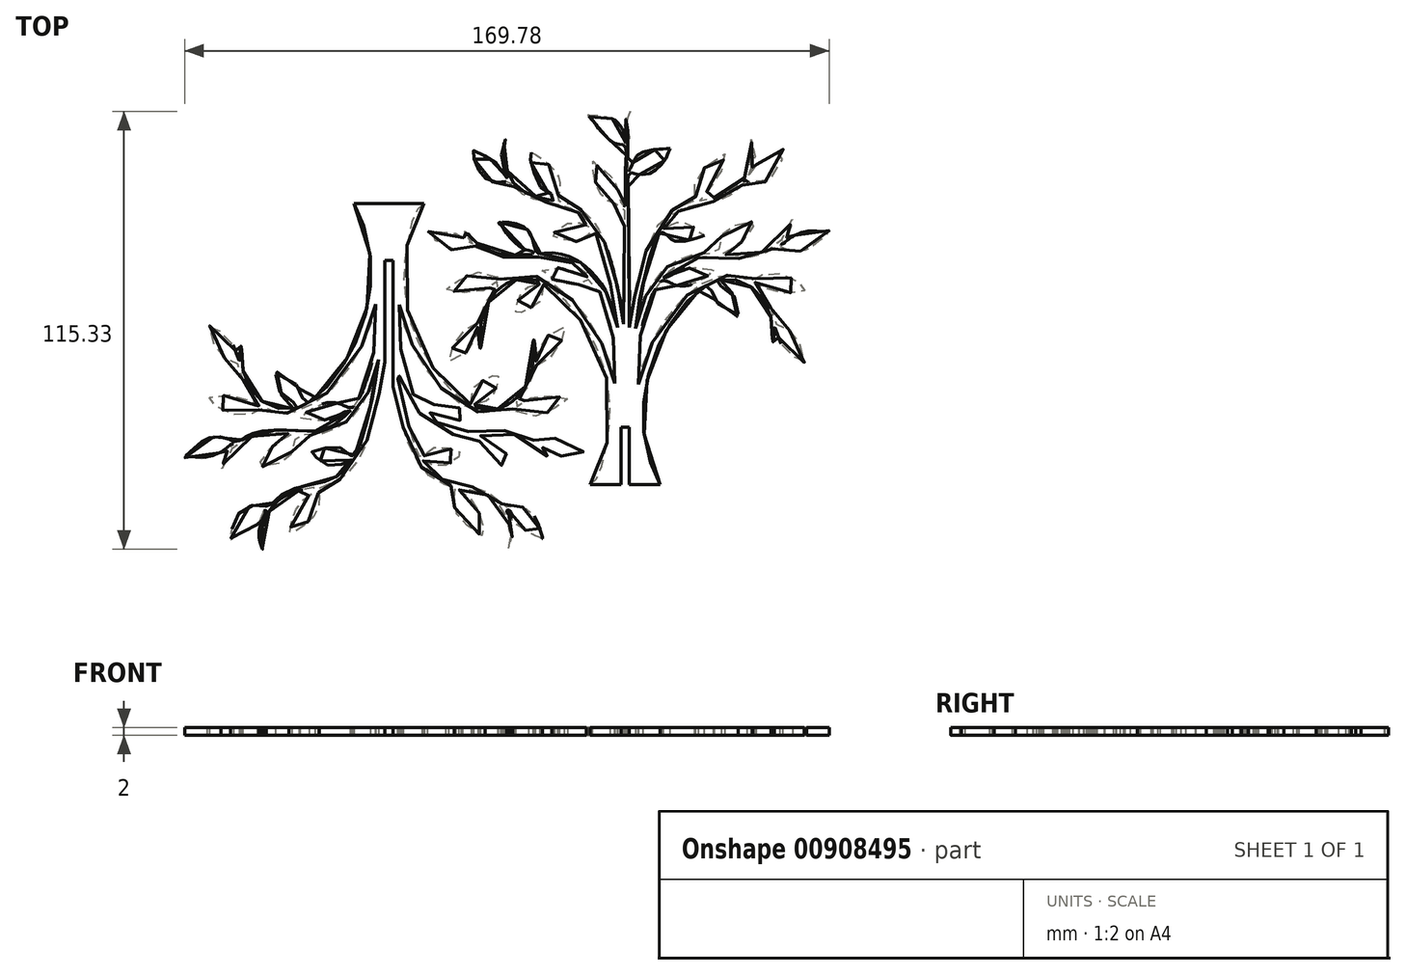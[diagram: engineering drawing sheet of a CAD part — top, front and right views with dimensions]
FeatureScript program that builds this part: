
annotation { "Feature Type Name" : "Feature", "Feature Type Description" : "" }
export const myFeature = defineFeature(function(context is Context, id is Id, definition is map)
    precondition{}
    {
        {
            var Q0;
            Q0=qCreatedBy(makeId("Top.planeOp"),FACE);
            var sketch = newSketch(context, id + "F0", { "sketchPlane" : qUnion([Q0])});
            skLineSegment(sketch, "E0", {"start": v(29.95, -44.14) * mm, "end": v(21.84, -44.14) * mm});
            skLineSegment(sketch, "E1.left", {"start": v(19.69, -28.94) * mm, "end": v(19.69, -44.14) * mm});
            skLineSegment(sketch, "E1.right", {"start": v(21.84, -28.94) * mm, "end": v(21.84, -44.14) * mm});
            skLineSegment(sketch, "E2", {"start": v(20.76, -44.14) * mm, "end": v(20.76, -22.34) * mm, "construction": true});
            skLineSegment(sketch, "E3.trimOffspring", {"start": v(19.69, -44.14) * mm, "end": v(11.58, -44.14) * mm});
            skLineSegment(sketch, "E4", {"start": v(19.69, -28.94) * mm, "end": v(21.84, -28.94) * mm});
            skFitSpline(sketch, "E5", {"points": [v(20.33, -1.79) * mm, v(20.33, 0) * mm, v(20.33, 5.52) * mm, v(20.5, 10.68) * mm, v(20.54, 16.14) * mm, v(20.63, 24.42) * mm, v(20.68, 28.14) * mm, v(20.56, 28.4) * mm, v(19.58, 29.1) * mm, v(18.8, 29.58) * mm, v(17.17, 30.16) * mm, v(15.4, 31.25) * mm, v(14.15, 32.69) * mm, v(13.3, 34.38) * mm, v(12.64, 36.54) * mm, v(12.27, 38.87) * mm, v(12.25, 41.19) * mm, v(12.34, 40.84) * mm, v(13.34, 39.96) * mm, v(15.38, 38.54) * mm, v(17.08, 37.03) * mm, v(18.33, 34.76) * mm, v(19.08, 32.67) * mm, v(19.54, 30.72) * mm, v(19.68, 30.05) * mm, v(19.94, 29.68) * mm, v(20.34, 29.42) * mm, v(20.66, 29.27) * mm, v(20.8, 29.32) * mm, v(20.82, 34.1) * mm, v(20.84, 38.03) * mm, v(20.98, 44.37) * mm, v(20.84, 44.72) * mm, v(20.33, 45.32) * mm, v(18.54, 45.7) * mm, v(16.85, 46.5) * mm, v(14.64, 48.66) * mm, v(13.71, 49.78) * mm, v(12.53, 51.47) * mm, v(11.78, 52.38) * mm, v(10.93, 53.24) * mm, v(11.32, 53.24) * mm, v(12.6, 53.24) * mm, v(14.97, 52.91) * mm, v(17.45, 52.24) * mm, v(18.96, 51.1) * mm, v(20.33, 48.85) * mm, v(20.77, 47.18) * mm, v(20.89, 46.37) * mm, v(20.89, 45.72) * mm, v(21.1, 45.58) * mm, v(21.3, 46.46) * mm, v(20.96, 49.08) * mm, v(20.77, 51.54) * mm, v(22.1, 54.21) * mm, v(21.9, 53.63) * mm, v(21.23, 51.98) * mm, v(21.26, 49.9) * mm, v(21.72, 47.8) * mm, v(21.8, 46.09) * mm, v(21.42, 44.58) * mm, v(21.51, 43.2) * mm, v(21.47, 40.89) * mm, v(21.5, 39.14) * mm, v(21.51, 38.22) * mm, v(21.82, 38.61) * mm, v(22.44, 40) * mm, v(23.44, 41.95) * mm, v(24.5, 43) * mm, v(25.83, 43.63) * mm, v(27.5, 44.02) * mm, v(29.7, 44.28) * mm, v(32.68, 44.37) * mm, v(32.54, 44.28) * mm, v(32.17, 43.49) * mm, v(31.5, 41.84) * mm, v(30.03, 39.86) * mm, v(28.57, 38.56) * mm, v(26.57, 37.66) * mm, v(24.62, 37.61) * mm, v(23.56, 37.73) * mm, v(22.37, 38.05) * mm, v(22.14, 37.82) * mm, v(21.51, 37.22) * mm, v(21.44, 35.85) * mm, v(21.56, 32.92) * mm, v(21.58, 30.11) * mm, v(21.65, 24.28) * mm, v(21.7, 18.8) * mm, v(21.77, 11.03) * mm, v(21.9, 6.5) * mm, v(21.84, 1.53) * mm, v(21.82, -2.7) * mm], "startDerivative": vector(0.58, 144) * mm, "endDerivative": vector(0.16, -253) * mm});
            skFitSpline(sketch, "E6", {"points": [v(21.82, -2.7) * mm, v(22.07, -2.06) * mm, v(22.19, -1.2) * mm, v(22.25, 0.23) * mm, v(22.62, 2.54) * mm, v(23.19, 5.31) * mm, v(24.24, 10.2) * mm, v(25.16, 13.53) * mm, v(26.2, 17.34) * mm, v(28.25, 22.4) * mm, v(30.9, 26.17) * mm, v(33.24, 28.2) * mm, v(35.34, 29.42) * mm, v(37.8, 30.2) * mm, v(39.05, 30.44) * mm, v(39.21, 30.93) * mm, v(39.4, 31.69) * mm, v(39.25, 32.25) * mm, v(39.08, 34.12) * mm, v(39.34, 36.05) * mm, v(40.13, 37.73) * mm, v(41.68, 39.4) * mm, v(43.71, 41.14) * mm, v(45.25, 42.16) * mm, v(47.1, 43.05) * mm, v(46.96, 42.79) * mm, v(46.63, 41.37) * mm, v(46.27, 39.34) * mm, v(45.35, 36.8) * mm, v(44.33, 35.1) * mm, v(42.04, 32.93) * mm, v(40.66, 31.98) * mm, v(40.27, 31.45) * mm, v(40.17, 30.74) * mm, v(40.5, 30.67) * mm, v(42.46, 31.1) * mm, v(45.1, 31.62) * mm, v(47.45, 32.57) * mm, v(49.75, 33.99) * mm, v(51.46, 35.66) * mm, v(52.68, 37.6) * mm, v(53.56, 39.53) * mm, v(54.15, 41.3) * mm, v(54.38, 43.5) * mm, v(54.02, 46.92) * mm, v(54.32, 46.36) * mm, v(54.78, 44.85) * mm, v(54.97, 42.65) * mm, v(54.38, 39.8) * mm, v(53.17, 37.3) * mm, v(53.02, 36.83) * mm, v(53.39, 36.67) * mm, v(53.82, 36.97) * mm, v(54.48, 38.65) * mm, v(55.53, 40.39) * mm, v(58.16, 42.1) * mm, v(60.33, 43.08) * mm, v(62.03, 44) * mm, v(62.3, 44.5) * mm, v(62.4, 43.54) * mm, v(61.77, 40.62) * mm, v(60.65, 37.93) * mm, v(58.52, 36.02) * mm, v(56.09, 35.27) * mm, v(53.8, 35.3) * mm, v(53, 35.73) * mm, v(52.64, 35.99) * mm, v(52.38, 36.02) * mm, v(52.12, 35.63) * mm, v(50.93, 34.22) * mm, v(49.33, 32.87) * mm, v(47.65, 31.69) * mm, v(45.62, 30.93) * mm, v(43.48, 30.37) * mm, v(39.84, 29.68) * mm, v(38.65, 29.39) * mm, v(36.62, 28.76) * mm, v(34.81, 27.98) * mm, v(33.3, 26.9) * mm, v(32.38, 26.04) * mm, v(31, 24.66) * mm, v(30.31, 23.64) * mm, v(30.58, 23.38) * mm, v(30.97, 23.38) * mm, v(31.99, 24.04) * mm, v(33.8, 24.76) * mm, v(35.3, 25.12) * mm, v(37.93, 24.23) * mm, v(39.34, 23.22) * mm, v(40.62, 22.13) * mm, v(41.6, 21.57) * mm, v(40.89, 21.25) * mm, v(39.11, 20.69) * mm, v(36.72, 20.1) * mm, v(34.52, 20.03) * mm, v(32.97, 20.5) * mm, v(31.04, 22.16) * mm, v(29.64, 22.16) * mm, v(28.74, 20.46) * mm, v(27.36, 16.22) * mm, v(25.5, 8.8) * mm, v(24.67, 5.06) * mm, v(24, 0.79) * mm, v(23.48, -2.99) * mm], "startDerivative": vector(50.29, 106) * mm, "endDerivative": vector(-37.17, -267.82) * mm});
            skFitSpline(sketch, "E7", {"points": [v(23.48, -2.99) * mm, v(23.78, -2.7) * mm, v(24.1, -1.08) * mm, v(24.67, 1.95) * mm, v(26.08, 5.29) * mm, v(27.59, 8.18) * mm, v(28.48, 9.59) * mm, v(30.7, 12.25) * mm, v(33.33, 14.35) * mm, v(36.55, 16.06) * mm, v(39.77, 16.85) * mm, v(42.73, 16.91) * mm, v(45.06, 16.75) * mm, v(45.52, 17.53) * mm, v(45.65, 19.28) * mm, v(46.63, 22.03) * mm, v(47.78, 23.35) * mm, v(49.56, 24.27) * mm, v(52.18, 24.99) * mm, v(55.33, 25.15) * mm, v(55.04, 24.92) * mm, v(54.48, 23.84) * mm, v(52.6, 21.25) * mm, v(51.2, 19.57) * mm, v(49.13, 18.06) * mm, v(46.38, 17.29) * mm, v(46.21, 16.81) * mm, v(46.34, 16.52) * mm, v(47.75, 16.45) * mm, v(50.5, 16.32) * mm, v(53.7, 16.48) * mm, v(56.16, 16.98) * mm, v(59.08, 18.22) * mm, v(61.4, 20.03) * mm, v(63.41, 22.2) * mm, v(65.02, 26.66) * mm, v(64.99, 26.14) * mm, v(64.73, 24.33) * mm, v(63.87, 21.93) * mm, v(62.76, 20.42) * mm, v(61.61, 19.48) * mm, v(61.62, 19.3) * mm, v(61.74, 19.2) * mm, v(62.3, 19.3) * mm, v(63.97, 20.65) * mm, v(67.71, 22.43) * mm, v(70.9, 22.7) * mm, v(73.4, 22.6) * mm, v(74.51, 22.82) * mm, v(73.36, 21.4) * mm, v(70.5, 18.98) * mm, v(68.6, 17.76) * mm, v(65.32, 17.3) * mm, v(62.76, 18.03) * mm, v(61.97, 18.49) * mm, v(60.65, 18.65) * mm, v(59.9, 18.2) * mm, v(58.59, 17.37) * mm, v(56.85, 16.58) * mm, v(53.89, 15.8) * mm, v(49.5, 15.5) * mm, v(45.06, 15.66) * mm, v(42.17, 15.86) * mm, v(39.84, 15.73) * mm, v(36.75, 14.9) * mm, v(34.02, 13.36) * mm, v(30.87, 10.48) * mm, v(31, 10.48) * mm, v(31.71, 10.5) * mm, v(33.3, 11.33) * mm, v(35.8, 12.54) * mm, v(37.7, 12.94) * mm, v(40.72, 12.9) * mm, v(44.3, 12.28) * mm, v(43.8, 12.18) * mm, v(42.6, 10.93) * mm, v(40.4, 9.65) * mm, v(37.93, 8.54) * mm, v(35.93, 8.24) * mm, v(33.93, 8.54) * mm, v(32.07, 9.3) * mm, v(31.3, 9.56) * mm, v(30.4, 9.58) * mm, v(29.82, 9.06) * mm, v(28.15, 6.37) * mm, v(27.2, 4) * mm, v(25.13, -2.7) * mm, v(24.44, -7.85) * mm, v(24.24, -14.25) * mm, v(24.27, -17.63) * mm], "startDerivative": vector(65.15, 43.2) * mm, "endDerivative": vector(4.6, -218.26) * mm});
            skFitSpline(sketch, "E8", {"points": [v(24.27, -17.63) * mm, v(24.67, -15.33) * mm, v(26.47, -9.72) * mm, v(28.21, -5.98) * mm, v(32.42, 0.66) * mm, v(37.24, 6.04) * mm, v(41.12, 9) * mm, v(45.12, 10.67) * mm, v(49.06, 11.03) * mm, v(51.79, 10.38) * mm, v(53, 9.65) * mm, v(53.66, 9.65) * mm, v(54.97, 10.11) * mm, v(56.88, 11.2) * mm, v(60.16, 11.76) * mm, v(63.35, 10.87) * mm, v(66.8, 9) * mm, v(68.6, 7.39) * mm, v(68.24, 6.96) * mm, v(64.53, 6.47) * mm, v(60.65, 6.4) * mm, v(56.78, 8.18) * mm, v(55.56, 9.09) * mm, v(54.72, 9.07) * mm, v(54.37, 8.75) * mm, v(55.2, 8) * mm, v(57.63, 5.32) * mm, v(59.2, 1.95) * mm, v(60.03, -1.15) * mm, v(60.95, -2.13) * mm, v(62.3, -2.7) * mm, v(64.89, -4.07) * mm, v(66.5, -6.44) * mm, v(67.29, -9) * mm, v(67.98, -11.92) * mm, v(67.75, -11.69) * mm, v(65.8, -10.74) * mm, v(63.12, -9.06) * mm, v(61.11, -5.06) * mm, v(60.4, -2.99) * mm, v(60.15, -2.76) * mm, v(60.1, -3.6) * mm, v(60.1, -4.47) * mm, v(60, -5.5) * mm, v(59.24, -7.75) * mm, v(59.34, -6.86) * mm, v(59.67, -3.41) * mm, v(59.14, 0) * mm, v(58.29, 2.66) * mm, v(56.88, 5.19) * mm, v(55.27, 6.9) * mm, v(52.84, 8.83) * mm, v(50.87, 9.65) * mm, v(48.64, 10.02) * mm, v(46.5, 10.02) * mm, v(44.02, 9.27) * mm, v(44.32, 8.94) * mm, v(45.45, 8.4) * mm, v(47.75, 7.52) * mm, v(49.36, 5.81) * mm, v(50.08, 3.61) * mm, v(50.48, 1.28) * mm, v(50.44, -0.46) * mm, v(50.18, 0.4) * mm, v(49, 1.38) * mm, v(46.73, 2.43) * mm, v(44.7, 3.9) * mm, v(43.88, 4.96) * mm, v(43.55, 7.2) * mm, v(43.35, 8.4) * mm, v(42.99, 8.77) * mm, v(41.94, 8.2) * mm, v(38.72, 5.78) * mm, v(34.58, 1.08) * mm, v(31.8, -3.25) * mm, v(29.6, -7.52) * mm, v(27.03, -14.51) * mm, v(25.88, -20.59) * mm, v(25.5, -27.19) * mm, v(26.28, -33.72) * mm, v(28.48, -41.34) * mm, v(29.95, -44.14) * mm], "startDerivative": vector(20.26, 170.29) * mm, "endDerivative": vector(107.17, -173.54) * mm});
            skFitSpline(sketch, "E9", {"points": [v(11.58, -44.14) * mm, v(12.57, -43.27) * mm, v(13.81, -41.62) * mm, v(15.55, -35.41) * mm, v(16.71, -27.3) * mm, v(16.46, -19.53) * mm, v(13.73, -9.18) * mm, v(10.42, -2.98) * mm, v(7.36, 1.57) * mm, v(2.73, 6.54) * mm, v(-0.58, 8.69) * mm, v(-1.14, 7.83) * mm, v(-1.16, 5.96) * mm, v(-1.43, 4.58) * mm, v(-2.54, 3.48) * mm, v(-4.3, 2.32) * mm, v(-6.84, 1.16) * mm, v(-8, 0.94) * mm, v(-8.06, 1.27) * mm, v(-7.9, 2.87) * mm, v(-7.23, 5.14) * mm, v(-6.3, 6.85) * mm, v(-5.02, 7.9) * mm, v(-3.48, 8.45) * mm, v(-2, 8.65) * mm, v(-1.68, 9.02) * mm, v(-1.82, 9.35) * mm, v(-2.77, 9.73) * mm, v(-3.65, 9.89) * mm, v(-5.72, 10.08) * mm, v(-7.71, 9.97) * mm, v(-9.9, 9.15) * mm, v(-12, 7.82) * mm, v(-14.47, 5.32) * mm, v(-15.52, 3.37) * mm, v(-16.62, 0.71) * mm, v(-17.28, -2.76) * mm, v(-17.36, -8.3) * mm, v(-17.6, -7.45) * mm, v(-17.87, -5.4) * mm, v(-17.84, -4.07) * mm, v(-17.78, -2.78) * mm, v(-17.91, -2.52) * mm, v(-18.34, -2.9) * mm, v(-18.67, -3.84) * mm, v(-19, -5.93) * mm, v(-19.7, -7.72) * mm, v(-21.07, -9.29) * mm, v(-22.7, -10.38) * mm, v(-25.6, -11.63) * mm, v(-25.44, -11.35) * mm, v(-25.17, -10.07) * mm, v(-24.5, -7.33) * mm, v(-23.14, -4.52) * mm, v(-20.48, -2.84) * mm, v(-18.53, -1.9) * mm, v(-17.75, -1.16) * mm, v(-17.32, 0.13) * mm, v(-16.15, 3.68) * mm, v(-13.8, 7.12) * mm, v(-12.59, 8.16) * mm, v(-11.95, 8.73) * mm, v(-12, 9.04) * mm, v(-12.4, 9.31) * mm, v(-13.26, 9.23) * mm, v(-14.27, 8.29) * mm, v(-16.7, 7) * mm, v(-19.31, 6.37) * mm, v(-21.7, 6.5) * mm, v(-24, 6.76) * mm, v(-26.38, 7.35) * mm, v(-26.14, 7.5) * mm, v(-24.27, 8.99) * mm, v(-22.36, 10.12) * mm, v(-19.35, 11.64) * mm, v(-15.91, 11.76) * mm, v(-13.69, 11.02) * mm, v(-12.2, 10.16) * mm, v(-11.14, 9.88) * mm, v(-9.14, 10.35) * mm, v(-7.3, 10.87) * mm, v(-3.46, 10.86) * mm, v(-0.26, 9.93) * mm, v(3.69, 7.43) * mm, v(6.15, 5.28) * mm, v(9.04, 1.96) * mm, v(12.63, -3.2) * mm, v(14.82, -7.37) * mm, v(16.1, -10.53) * mm, v(17.36, -14.17) * mm, v(18.06, -17.49) * mm], "startDerivative": vector(118.06, 97.69) * mm, "endDerivative": vector(43.29, -243.59) * mm});
            skFitSpline(sketch, "E10", {"points": [v(18.06, -17.49) * mm, v(18.06, -16.28) * mm, v(18.06, -11.54) * mm, v(17.75, -6.34) * mm, v(17.22, -3.16) * mm, v(16.4, 0.74) * mm, v(14.3, 6.24) * mm, v(12.4, 9.38) * mm, v(11.9, 9.76) * mm, v(10.93, 9.83) * mm, v(10.02, 9.4) * mm, v(8.88, 8.75) * mm, v(8.02, 8.5) * mm, v(6.58, 8.38) * mm, v(5.07, 8.43) * mm, v(3.75, 8.91) * mm, v(1.96, 9.8) * mm, v(0.62, 10.63) * mm, v(-1.33, 12.26) * mm, v(-1.03, 12.35) * mm, v(0.25, 12.72) * mm, v(2.6, 13.05) * mm, v(5.33, 12.95) * mm, v(7.35, 12.4) * mm, v(9.11, 11.5) * mm, v(9.98, 11) * mm, v(10.93, 10.57) * mm, v(11.22, 10.55) * mm, v(11.33, 10.68) * mm, v(11.05, 11.04) * mm, v(10.72, 11.33) * mm, v(9.28, 12.68) * mm, v(7.72, 13.74) * mm, v(5.47, 14.97) * mm, v(3.36, 15.67) * mm, v(1.5, 15.88) * mm, v(-0.87, 15.95) * mm, v(-3.42, 15.72) * mm, v(-4.89, 15.74) * mm, v(-8.72, 15.67) * mm, v(-10.53, 15.79) * mm, v(-12.27, 16.02) * mm, v(-14.03, 16.5) * mm, v(-16.54, 17.64) * mm, v(-17.79, 18.44) * mm, v(-18.46, 18.76) * mm, v(-19.01, 18.74) * mm, v(-19.91, 18.6) * mm, v(-20.47, 18.3) * mm, v(-21.25, 17.95) * mm, v(-23.34, 17.67) * mm, v(-25.04, 17.78) * mm, v(-27.6, 19.1) * mm, v(-29.33, 20.3) * mm, v(-30.54, 21.29) * mm, v(-31.28, 22.38) * mm, v(-30.94, 22.57) * mm, v(-28.87, 22.87) * mm, v(-26.15, 22.78) * mm, v(-23.3, 21.82) * mm, v(-20.9, 20.31) * mm, v(-20.13, 19.65) * mm, v(-19.47, 19.41) * mm, v(-19.26, 19.55) * mm, v(-19.49, 19.9) * mm, v(-20.16, 20.6) * mm, v(-21.4, 22.38) * mm, v(-22.3, 24.3) * mm, v(-22.14, 24.26) * mm, v(-21.77, 23.66) * mm, v(-20.49, 21.73) * mm, v(-18, 19.32) * mm, v(-16.3, 18.18) * mm, v(-12.64, 16.72) * mm, v(-9.11, 16.4) * mm, v(-6, 16.48) * mm, v(-3.67, 16.62) * mm, v(-3.41, 17) * mm, v(-3.62, 17.28) * mm, v(-4.05, 17.46) * mm, v(-5.68, 17.83) * mm, v(-7.79, 19.13) * mm, v(-10.27, 21.92) * mm, v(-11.87, 24.12) * mm, v(-12.57, 25.1) * mm, v(-12.32, 25.1) * mm, v(-11.1, 25.14) * mm, v(-8.7, 24.82) * mm, v(-6.07, 23.98) * mm, v(-4.19, 22.06) * mm, v(-3.4, 19.8) * mm, v(-2.94, 17.78) * mm, v(-2.7, 17.27) * mm, v(-2.12, 16.79) * mm, v(-0.54, 16.92) * mm, v(2.68, 16.85) * mm, v(5.91, 16.09) * mm, v(9.37, 14.16) * mm, v(11.58, 12.26) * mm, v(13.41, 10.28) * mm, v(15.27, 7.45) * mm, v(16.47, 4.94) * mm, v(17.47, 2.3) * mm, v(18.38, -0.74) * mm, v(18.8, -2.7) * mm], "startDerivative": vector(-0.6, 126.61) * mm, "endDerivative": vector(34.6, -179.6) * mm});
            skFitSpline(sketch, "E11", {"points": [v(18.8, -2.7) * mm, v(18.8, -1.02) * mm, v(18.3, 1.95) * mm, v(17.61, 5.9) * mm, v(16.22, 11.7) * mm, v(15.27, 15.55) * mm, v(13.32, 21.5) * mm, v(12.79, 22.53) * mm, v(12.05, 22.88) * mm, v(11.58, 22.45) * mm, v(10.93, 21.7) * mm, v(9.74, 20.64) * mm, v(8.51, 20.04) * mm, v(6.35, 20.08) * mm, v(3.9, 20.69) * mm, v(2.5, 21.22) * mm, v(1.3, 21.5) * mm, v(1.4, 21.68) * mm, v(2.61, 22.82) * mm, v(4.8, 24.4) * mm, v(6.96, 25) * mm, v(8.86, 24.87) * mm, v(10.47, 24.31) * mm, v(11.29, 23.79) * mm, v(11.82, 23.65) * mm, v(11.9, 23.99) * mm, v(11.47, 24.78) * mm, v(10.78, 25.56) * mm, v(9.02, 27.14) * mm, v(6.68, 28.56) * mm, v(4.91, 29.18) * mm, v(2.85, 29.7) * mm, v(0.6, 30.16) * mm, v(-1.1, 30.48) * mm, v(-3.3, 31.11) * mm, v(-5.19, 31.85) * mm, v(-7.1, 33) * mm, v(-9.07, 35.01) * mm, v(-9.55, 35.55) * mm, v(-10.25, 35.75) * mm, v(-10.98, 35.72) * mm, v(-11.88, 35.6) * mm, v(-13.01, 35.49) * mm, v(-14.34, 35.75) * mm, v(-15.9, 36.45) * mm, v(-16.77, 37.17) * mm, v(-17.75, 38.56) * mm, v(-18.51, 40.12) * mm, v(-19.21, 42.12) * mm, v(-19.68, 44.11) * mm, v(-19.37, 43.95) * mm, v(-18.6, 43.72) * mm, v(-16.73, 42.81) * mm, v(-14.78, 41.65) * mm, v(-12.85, 40.37) * mm, v(-11.78, 39.21) * mm, v(-11.6, 38.12) * mm, v(-11.24, 36.92) * mm, v(-10.5, 36.58) * mm, v(-10.3, 36.86) * mm, v(-10.46, 37.33) * mm, v(-10.8, 38.24) * mm, v(-11.6, 40.84) * mm, v(-11.74, 43.65) * mm, v(-10.8, 46.85) * mm, v(-10.9, 46.34) * mm, v(-11.34, 43.65) * mm, v(-11, 40.35) * mm, v(-10.1, 38.03) * mm, v(-8.58, 35.34) * mm, v(-6.14, 33.18) * mm, v(-4.28, 32.3) * mm, v(-1.31, 31.39) * mm, v(0.96, 30.95) * mm, v(2.07, 30.73) * mm, v(2.22, 31.2) * mm, v(1.45, 32.35) * mm, v(0.18, 32.92) * mm, v(-1.48, 34.32) * mm, v(-2.7, 36.54) * mm, v(-3.59, 39.1) * mm, v(-4.17, 41.33) * mm, v(-4.54, 43.79) * mm, v(-4.35, 43.72) * mm, v(-3.17, 43.04) * mm, v(-0.52, 41.19) * mm, v(1.45, 39.47) * mm, v(2.85, 37.7) * mm, v(3.57, 35.03) * mm, v(3.43, 33) * mm, v(3.1, 32.02) * mm, v(3.05, 31.19) * mm, v(3.46, 30.6) * mm, v(4.2, 30.27) * mm, v(5.63, 29.97) * mm, v(8.02, 29.07) * mm, v(10.79, 26.95) * mm, v(12.2, 25.4) * mm, v(14.1, 22.43) * mm, v(15.4, 19.52) * mm, v(16.96, 14.86) * mm, v(17.73, 12.07) * mm, v(18.56, 8.5) * mm, v(19.47, 4.57) * mm, v(19.84, 2.34) * mm, v(20.14, -0.14) * mm, v(20.3, -1.77) * mm, v(20.33, -1.79) * mm], "startDerivative": vector(9.23, 171.99) * mm, "endDerivative": vector(18.47, -7.81) * mm});
            skSolve(sketch);
        }
        {
            var Q0;
            Q0=makeQuery(id+"F0.imprint","IMPRINT",FACE,{"disambiguationData":[TD([[makeQuery(id+"F0.imprint","IMPRINT",EDGE,{"derivedFrom":sQuery(id+"F0.wireOp",EDGE,"E0")}),-1.0]])]});
            extrude(context, id + "F1", {"entities" : qUnion([Q0]), "depth" : 2 * mm, "offsetDistance" : 25 * mm});
        }
        {
            var Q0;
            Q0=qCreatedBy(makeId("Top.planeOp"),FACE);
            var sketch = newSketch(context, id + "F2", { "sketchPlane" : qUnion([Q0])});
            skLineSegment(sketch, "E12", {"start": v(-50.68, 29.94) * mm, "end": v(-42.5, 29.94) * mm});
            skLineSegment(sketch, "E13.bottom", {"start": v(-40.42, 15) * mm, "end": v(-42.57, 15) * mm});
            skLineSegment(sketch, "E14", {"start": v(-41.5, 29.94) * mm, "end": v(-41.5, 8.15) * mm, "construction": true});
            skLineSegment(sketch, "E15.trimOffspring", {"start": v(-42.5, 29.94) * mm, "end": v(-32.32, 29.94) * mm});
            skLineSegment(sketch, "E16.left", {"start": v(-42.57, 15) * mm, "end": v(-42.57, -11.83) * mm});
            skLineSegment(sketch, "E16.right", {"start": v(-40.42, 15) * mm, "end": v(-40.42, -18.28) * mm});
            skFitSpline(sketch, "E17", {"points": [v(-42.44, -11.54) * mm, v(-42.72, -12.17) * mm, v(-42.94, -12.99) * mm, v(-42.99, -14.42) * mm, v(-43.35, -16.74) * mm, v(-43.93, -19.51) * mm, v(-44.98, -24.4) * mm, v(-45.9, -27.73) * mm, v(-46.95, -31.53) * mm, v(-48.98, -36.6) * mm, v(-51.64, -40.37) * mm, v(-53.97, -42.4) * mm, v(-56.07, -43.62) * mm, v(-58.54, -44.4) * mm, v(-59.78, -44.64) * mm, v(-59.95, -45.13) * mm, v(-60.15, -45.88) * mm, v(-59.98, -46.44) * mm, v(-59.82, -48.31) * mm, v(-60.08, -50.25) * mm, v(-60.87, -51.92) * mm, v(-62.41, -53.6) * mm, v(-64.45, -55.34) * mm, v(-65.99, -56.36) * mm, v(-67.83, -57.24) * mm, v(-67.7, -56.98) * mm, v(-67.37, -55.57) * mm, v(-67, -53.53) * mm, v(-66.09, -51) * mm, v(-65.07, -49.3) * mm, v(-62.77, -47.13) * mm, v(-61.4, -46.18) * mm, v(-61.01, -45.65) * mm, v(-60.9, -44.93) * mm, v(-61.23, -44.87) * mm, v(-63.2, -45.3) * mm, v(-65.83, -45.82) * mm, v(-68.19, -46.77) * mm, v(-70.49, -48.18) * mm, v(-72.2, -49.86) * mm, v(-73.41, -51.8) * mm, v(-74.3, -53.73) * mm, v(-74.89, -55.5) * mm, v(-75.12, -57.7) * mm, v(-74.76, -61.12) * mm, v(-75.05, -60.56) * mm, v(-75.51, -59.05) * mm, v(-75.7, -56.85) * mm, v(-75.12, -54) * mm, v(-73.9, -51.5) * mm, v(-73.76, -51.02) * mm, v(-74.12, -50.87) * mm, v(-74.56, -51.17) * mm, v(-75.22, -52.84) * mm, v(-76.27, -54.58) * mm, v(-78.9, -56.3) * mm, v(-81.06, -57.28) * mm, v(-82.77, -58.2) * mm, v(-83.03, -58.69) * mm, v(-83.13, -57.74) * mm, v(-82.5, -54.81) * mm, v(-81.39, -52.12) * mm, v(-79.26, -50.22) * mm, v(-76.83, -49.46) * mm, v(-74.53, -49.5) * mm, v(-73.74, -49.92) * mm, v(-73.38, -50.18) * mm, v(-73.12, -50.22) * mm, v(-72.85, -49.82) * mm, v(-71.67, -48.41) * mm, v(-70.06, -47.07) * mm, v(-68.39, -45.88) * mm, v(-66.35, -45.13) * mm, v(-64.22, -44.57) * mm, v(-60.57, -43.88) * mm, v(-59.39, -43.58) * mm, v(-57.35, -42.96) * mm, v(-55.55, -42.17) * mm, v(-54.04, -41.09) * mm, v(-53.12, -40.24) * mm, v(-51.74, -38.86) * mm, v(-51.05, -37.84) * mm, v(-51.31, -37.58) * mm, v(-51.7, -37.58) * mm, v(-52.72, -38.23) * mm, v(-54.53, -38.95) * mm, v(-56.04, -39.32) * mm, v(-58.67, -38.43) * mm, v(-60.08, -37.41) * mm, v(-61.36, -36.33) * mm, v(-62.35, -35.77) * mm, v(-61.62, -35.44) * mm, v(-59.85, -34.88) * mm, v(-57.45, -34.3) * mm, v(-55.25, -34.23) * mm, v(-53.7, -34.69) * mm, v(-51.77, -36.36) * mm, v(-50.38, -36.36) * mm, v(-49.47, -34.65) * mm, v(-48.1, -30.42) * mm, v(-46.24, -23) * mm, v(-45.4, -19.25) * mm, v(-44.75, -14.98) * mm, v(-44.22, -11.2) * mm], "startDerivative": vector(-50.25, -106) * mm, "endDerivative": vector(37.17, 267.82) * mm});
            skFitSpline(sketch, "E18", {"points": [v(-44.22, -11.2) * mm, v(-44.52, -11.5) * mm, v(-44.84, -13.11) * mm, v(-45.4, -16.14) * mm, v(-46.81, -19.48) * mm, v(-48.32, -22.37) * mm, v(-49.21, -23.78) * mm, v(-51.44, -26.44) * mm, v(-54.07, -28.55) * mm, v(-57.29, -30.25) * mm, v(-60.5, -31.04) * mm, v(-63.46, -31.1) * mm, v(-65.8, -30.94) * mm, v(-66.25, -31.73) * mm, v(-66.38, -33.47) * mm, v(-67.37, -36.23) * mm, v(-68.52, -37.54) * mm, v(-70.3, -38.46) * mm, v(-72.92, -39.18) * mm, v(-76.07, -39.35) * mm, v(-75.77, -39.12) * mm, v(-75.22, -38.04) * mm, v(-73.35, -35.44) * mm, v(-71.93, -33.77) * mm, v(-69.86, -32.26) * mm, v(-67.11, -31.48) * mm, v(-66.95, -31) * mm, v(-67.07, -30.71) * mm, v(-68.49, -30.65) * mm, v(-71.24, -30.52) * mm, v(-74.43, -30.68) * mm, v(-76.9, -31.17) * mm, v(-79.81, -32.42) * mm, v(-82.14, -34.23) * mm, v(-84.15, -36.4) * mm, v(-85.76, -40.86) * mm, v(-85.72, -40.33) * mm, v(-85.46, -38.53) * mm, v(-84.6, -36.13) * mm, v(-83.5, -34.62) * mm, v(-82.35, -33.67) * mm, v(-82.36, -33.5) * mm, v(-82.47, -33.4) * mm, v(-83.03, -33.5) * mm, v(-84.7, -34.85) * mm, v(-88.45, -36.62) * mm, v(-91.63, -36.89) * mm, v(-94.13, -36.79) * mm, v(-95.25, -37.02) * mm, v(-94.1, -35.6) * mm, v(-91.24, -33.18) * mm, v(-89.34, -31.96) * mm, v(-86.05, -31.5) * mm, v(-83.5, -32.22) * mm, v(-82.7, -32.68) * mm, v(-81.39, -32.85) * mm, v(-80.63, -32.39) * mm, v(-79.32, -31.57) * mm, v(-77.58, -30.78) * mm, v(-74.63, -30) * mm, v(-70.23, -29.7) * mm, v(-65.8, -29.86) * mm, v(-62.9, -30.06) * mm, v(-60.57, -29.93) * mm, v(-57.49, -29.1) * mm, v(-54.76, -27.56) * mm, v(-51.6, -24.67) * mm, v(-51.74, -24.67) * mm, v(-52.45, -24.7) * mm, v(-54.04, -25.53) * mm, v(-56.53, -26.74) * mm, v(-58.44, -27.13) * mm, v(-61.46, -27.1) * mm, v(-65.04, -26.48) * mm, v(-64.55, -26.38) * mm, v(-63.33, -25.13) * mm, v(-61.13, -23.85) * mm, v(-58.67, -22.73) * mm, v(-56.66, -22.44) * mm, v(-54.66, -22.73) * mm, v(-52.8, -23.5) * mm, v(-52.03, -23.76) * mm, v(-51.13, -23.77) * mm, v(-50.56, -23.26) * mm, v(-48.88, -20.57) * mm, v(-47.93, -18.2) * mm, v(-45.86, -11.5) * mm, v(-45.17, -6.35) * mm, v(-44.98, 0.05) * mm, v(-45, 3.44) * mm], "startDerivative": vector(-65.15, -43.2) * mm, "endDerivative": vector(-4.6, 218.26) * mm});
            skFitSpline(sketch, "E19", {"points": [v(-45, 3.44) * mm, v(-45.4, 1.14) * mm, v(-47.2, -4.48) * mm, v(-48.95, -8.22) * mm, v(-53.15, -14.85) * mm, v(-57.98, -20.24) * mm, v(-61.85, -23.2) * mm, v(-65.86, -24.87) * mm, v(-69.8, -25.23) * mm, v(-72.52, -24.57) * mm, v(-73.74, -23.85) * mm, v(-74.4, -23.85) * mm, v(-75.7, -24.31) * mm, v(-77.61, -25.4) * mm, v(-80.9, -25.95) * mm, v(-84.08, -25.07) * mm, v(-87.53, -23.2) * mm, v(-89.34, -21.58) * mm, v(-88.97, -21.16) * mm, v(-85.26, -20.67) * mm, v(-81.39, -20.6) * mm, v(-77.52, -22.37) * mm, v(-76.3, -23.29) * mm, v(-75.46, -23.27) * mm, v(-75.1, -22.95) * mm, v(-75.94, -22.2) * mm, v(-78.37, -19.52) * mm, v(-79.94, -16.14) * mm, v(-80.77, -13.05) * mm, v(-81.69, -12.06) * mm, v(-83.03, -11.5) * mm, v(-85.63, -10.13) * mm, v(-87.23, -7.76) * mm, v(-88.02, -5.2) * mm, v(-88.71, -2.28) * mm, v(-88.48, -2.5) * mm, v(-86.54, -3.46) * mm, v(-83.85, -5.13) * mm, v(-81.85, -9.14) * mm, v(-81.13, -11.2) * mm, v(-80.9, -11.44) * mm, v(-80.84, -10.59) * mm, v(-80.83, -9.73) * mm, v(-80.73, -8.7) * mm, v(-79.98, -6.45) * mm, v(-80.08, -7.33) * mm, v(-80.4, -10.78) * mm, v(-79.88, -14.2) * mm, v(-79.03, -16.86) * mm, v(-77.61, -19.38) * mm, v(-76, -21.1) * mm, v(-73.57, -23.03) * mm, v(-71.6, -23.85) * mm, v(-69.37, -24.21) * mm, v(-67.24, -24.21) * mm, v(-64.75, -23.47) * mm, v(-65.05, -23.14) * mm, v(-66.19, -22.6) * mm, v(-68.49, -21.72) * mm, v(-70.1, -20) * mm, v(-70.82, -17.8) * mm, v(-71.21, -15.48) * mm, v(-71.18, -13.74) * mm, v(-70.92, -14.6) * mm, v(-69.73, -15.58) * mm, v(-67.47, -16.63) * mm, v(-65.43, -18.1) * mm, v(-64.61, -19.15) * mm, v(-64.28, -21.39) * mm, v(-64.09, -22.6) * mm, v(-63.72, -22.96) * mm, v(-62.67, -22.4) * mm, v(-59.46, -19.98) * mm, v(-55.32, -15.28) * mm, v(-52.53, -10.95) * mm, v(-50.33, -6.68) * mm, v(-47.77, 0.32) * mm, v(-46.62, 6.4) * mm, v(-46.24, 13) * mm, v(-47.01, 19.53) * mm, v(-49.21, 27.14) * mm, v(-50.68, 29.94) * mm], "startDerivative": vector(-20.26, -170.29) * mm, "endDerivative": vector(-107.17, 173.54) * mm});
            skFitSpline(sketch, "E20", {"points": [v(-32.32, 29.94) * mm, v(-33.3, 29.08) * mm, v(-34.55, 27.42) * mm, v(-36.29, 21.22) * mm, v(-37.45, 13.1) * mm, v(-37.2, 5.33) * mm, v(-34.47, -5.01) * mm, v(-31.16, -11.22) * mm, v(-28.1, -15.77) * mm, v(-23.46, -20.73) * mm, v(-20.15, -22.88) * mm, v(-19.6, -22.03) * mm, v(-19.58, -20.16) * mm, v(-19.3, -18.78) * mm, v(-18.2, -17.68) * mm, v(-16.43, -16.52) * mm, v(-13.9, -15.36) * mm, v(-12.73, -15.14) * mm, v(-12.68, -15.47) * mm, v(-12.84, -17.07) * mm, v(-13.5, -19.33) * mm, v(-14.44, -21.04) * mm, v(-15.71, -22.1) * mm, v(-17.26, -22.65) * mm, v(-18.73, -22.85) * mm, v(-19.06, -23.21) * mm, v(-18.91, -23.55) * mm, v(-17.97, -23.93) * mm, v(-17.08, -24.08) * mm, v(-15.01, -24.28) * mm, v(-13.02, -24.16) * mm, v(-10.84, -23.34) * mm, v(-8.73, -22.01) * mm, v(-6.27, -19.52) * mm, v(-5.21, -17.56) * mm, v(-4.12, -14.9) * mm, v(-3.46, -11.43) * mm, v(-3.38, -5.89) * mm, v(-3.14, -6.75) * mm, v(-2.87, -8.8) * mm, v(-2.9, -10.13) * mm, v(-2.95, -11.42) * mm, v(-2.82, -11.67) * mm, v(-2.4, -11.3) * mm, v(-2.07, -10.36) * mm, v(-1.74, -8.27) * mm, v(-1.03, -6.47) * mm, v(0.33, -4.91) * mm, v(1.97, -3.82) * mm, v(4.86, -2.57) * mm, v(4.7, -2.84) * mm, v(4.43, -4.13) * mm, v(3.77, -6.86) * mm, v(2.4, -9.67) * mm, v(-0.25, -11.35) * mm, v(-2.2, -12.3) * mm, v(-2.99, -13.03) * mm, v(-3.42, -14.32) * mm, v(-4.59, -17.88) * mm, v(-6.93, -21.31) * mm, v(-8.15, -22.36) * mm, v(-8.79, -22.92) * mm, v(-8.74, -23.24) * mm, v(-8.33, -23.5) * mm, v(-7.48, -23.43) * mm, v(-6.46, -22.48) * mm, v(-4.04, -21.2) * mm, v(-1.42, -20.57) * mm, v(0.96, -20.69) * mm, v(3.26, -20.96) * mm, v(5.64, -21.55) * mm, v(5.4, -21.7) * mm, v(3.53, -23.19) * mm, v(1.62, -24.32) * mm, v(-1.39, -25.84) * mm, v(-4.82, -25.96) * mm, v(-7.05, -25.22) * mm, v(-8.53, -24.36) * mm, v(-9.6, -24.07) * mm, v(-11.6, -24.55) * mm, v(-13.43, -25.07) * mm, v(-17.28, -25.06) * mm, v(-20.48, -24.12) * mm, v(-24.42, -21.62) * mm, v(-26.88, -19.48) * mm, v(-29.77, -16.16) * mm, v(-33.37, -11) * mm, v(-35.55, -6.82) * mm, v(-36.84, -3.66) * mm, v(-38.1, -0.03) * mm, v(-38.8, 3.29) * mm], "startDerivative": vector(-118.06, -97.69) * mm, "endDerivative": vector(-43.29, 243.59) * mm});
            skFitSpline(sketch, "E21", {"points": [v(-38.8, 3.29) * mm, v(-38.8, 2.08) * mm, v(-38.8, -2.66) * mm, v(-38.49, -7.86) * mm, v(-37.95, -11.04) * mm, v(-37.14, -14.94) * mm, v(-35.03, -20.44) * mm, v(-33.14, -23.58) * mm, v(-32.65, -23.95) * mm, v(-31.67, -24.02) * mm, v(-30.76, -23.6) * mm, v(-29.62, -22.95) * mm, v(-28.76, -22.7) * mm, v(-27.32, -22.58) * mm, v(-25.81, -22.62) * mm, v(-24.49, -23.11) * mm, v(-22.7, -24) * mm, v(-21.35, -24.83) * mm, v(-19.4, -26.45) * mm, v(-19.7, -26.55) * mm, v(-20.98, -26.92) * mm, v(-23.33, -27.24) * mm, v(-26.07, -27.15) * mm, v(-28.09, -26.6) * mm, v(-29.85, -25.69) * mm, v(-30.72, -25.19) * mm, v(-31.66, -24.77) * mm, v(-31.95, -24.74) * mm, v(-32.06, -24.87) * mm, v(-31.79, -25.24) * mm, v(-31.45, -25.52) * mm, v(-30.01, -26.87) * mm, v(-28.46, -27.94) * mm, v(-26.2, -29.17) * mm, v(-24.1, -29.87) * mm, v(-22.23, -30.08) * mm, v(-19.87, -30.15) * mm, v(-17.31, -29.91) * mm, v(-15.85, -29.94) * mm, v(-12.02, -29.87) * mm, v(-10.2, -29.98) * mm, v(-8.47, -30.22) * mm, v(-6.7, -30.7) * mm, v(-4.2, -31.84) * mm, v(-2.95, -32.63) * mm, v(-2.27, -32.95) * mm, v(-1.73, -32.94) * mm, v(-0.82, -32.8) * mm, v(-0.27, -32.5) * mm, v(0.52, -32.14) * mm, v(2.6, -31.86) * mm, v(4.3, -31.98) * mm, v(6.86, -33.3) * mm, v(8.6, -34.49) * mm, v(9.8, -35.49) * mm, v(10.55, -36.58) * mm, v(10.2, -36.76) * mm, v(8.13, -37.06) * mm, v(5.42, -36.97) * mm, v(2.56, -36.02) * mm, v(0.17, -34.51) * mm, v(-0.6, -33.85) * mm, v(-1.26, -33.61) * mm, v(-1.47, -33.75) * mm, v(-1.25, -34.1) * mm, v(-0.57, -34.79) * mm, v(0.66, -36.58) * mm, v(1.56, -38.5) * mm, v(1.4, -38.46) * mm, v(1.03, -37.85) * mm, v(-0.25, -35.93) * mm, v(-2.73, -33.51) * mm, v(-4.43, -32.37) * mm, v(-8.1, -30.91) * mm, v(-11.62, -30.59) * mm, v(-14.74, -30.68) * mm, v(-17.06, -30.82) * mm, v(-17.33, -31.19) * mm, v(-17.11, -31.48) * mm, v(-16.69, -31.65) * mm, v(-15.06, -32.03) * mm, v(-12.95, -33.33) * mm, v(-10.46, -36.11) * mm, v(-8.86, -38.32) * mm, v(-8.16, -39.3) * mm, v(-8.42, -39.3) * mm, v(-9.63, -39.34) * mm, v(-12.04, -39.01) * mm, v(-14.67, -38.18) * mm, v(-16.55, -36.25) * mm, v(-17.34, -34) * mm, v(-17.8, -31.98) * mm, v(-18.03, -31.47) * mm, v(-18.61, -30.98) * mm, v(-20.2, -31.12) * mm, v(-23.42, -31.05) * mm, v(-26.65, -30.28) * mm, v(-30.1, -28.36) * mm, v(-32.32, -26.45) * mm, v(-34.15, -24.48) * mm, v(-36, -21.65) * mm, v(-37.21, -19.14) * mm, v(-38.2, -16.5) * mm, v(-39.11, -13.45) * mm, v(-39.53, -11.5) * mm], "startDerivative": vector(0.6, -126.61) * mm, "endDerivative": vector(-34.6, 179.6) * mm});
            skFitSpline(sketch, "E22", {"points": [v(-39.53, -11.5) * mm, v(-39.53, -13.17) * mm, v(-39.05, -16.6) * mm, v(-38.35, -20.1) * mm, v(-36.96, -25.9) * mm, v(-36, -29.75) * mm, v(-34.05, -35.7) * mm, v(-33.52, -36.73) * mm, v(-32.78, -37.07) * mm, v(-32.32, -36.65) * mm, v(-31.66, -35.9) * mm, v(-30.48, -34.84) * mm, v(-29.25, -34.23) * mm, v(-27.09, -34.28) * mm, v(-24.63, -34.88) * mm, v(-23.23, -35.42) * mm, v(-22.03, -35.7) * mm, v(-22.14, -35.88) * mm, v(-23.35, -37.02) * mm, v(-25.53, -38.6) * mm, v(-27.7, -39.2) * mm, v(-29.6, -39.06) * mm, v(-31.2, -38.5) * mm, v(-32.02, -37.98) * mm, v(-32.55, -37.84) * mm, v(-32.64, -38.19) * mm, v(-32.2, -38.97) * mm, v(-31.52, -39.75) * mm, v(-29.76, -41.34) * mm, v(-27.41, -42.75) * mm, v(-25.65, -43.38) * mm, v(-23.58, -43.9) * mm, v(-21.33, -44.35) * mm, v(-19.63, -44.68) * mm, v(-17.43, -45.3) * mm, v(-15.55, -46.05) * mm, v(-13.64, -47.19) * mm, v(-11.67, -49.2) * mm, v(-11.18, -49.74) * mm, v(-10.48, -49.95) * mm, v(-9.76, -49.92) * mm, v(-8.86, -49.8) * mm, v(-7.72, -49.68) * mm, v(-6.4, -49.94) * mm, v(-4.84, -50.65) * mm, v(-3.96, -51.37) * mm, v(-2.99, -52.76) * mm, v(-2.22, -54.32) * mm, v(-1.52, -56.31) * mm, v(-1.06, -58.3) * mm, v(-1.36, -58.15) * mm, v(-2.13, -57.91) * mm, v(-4, -57) * mm, v(-5.96, -55.85) * mm, v(-7.89, -54.57) * mm, v(-8.95, -53.41) * mm, v(-9.14, -52.32) * mm, v(-9.5, -51.11) * mm, v(-10.23, -50.78) * mm, v(-10.43, -51.06) * mm, v(-10.28, -51.53) * mm, v(-9.93, -52.43) * mm, v(-9.14, -55.04) * mm, v(-9, -57.84) * mm, v(-9.93, -61.05) * mm, v(-9.84, -60.54) * mm, v(-9.4, -57.84) * mm, v(-9.74, -54.55) * mm, v(-10.63, -52.23) * mm, v(-12.16, -49.53) * mm, v(-14.6, -47.37) * mm, v(-16.45, -46.5) * mm, v(-19.43, -45.59) * mm, v(-21.7, -45.15) * mm, v(-22.8, -44.93) * mm, v(-22.96, -45.4) * mm, v(-22.18, -46.55) * mm, v(-20.91, -47.11) * mm, v(-19.26, -48.51) * mm, v(-18.03, -50.74) * mm, v(-17.15, -53.3) * mm, v(-16.57, -55.52) * mm, v(-16.2, -57.98) * mm, v(-16.38, -57.91) * mm, v(-17.57, -57.24) * mm, v(-20.21, -55.38) * mm, v(-22.19, -53.67) * mm, v(-23.58, -51.9) * mm, v(-24.3, -49.23) * mm, v(-24.16, -47.19) * mm, v(-23.84, -46.21) * mm, v(-23.79, -45.39) * mm, v(-24.2, -44.8) * mm, v(-24.94, -44.46) * mm, v(-26.37, -44.17) * mm, v(-28.76, -43.26) * mm, v(-31.52, -41.15) * mm, v(-32.94, -39.6) * mm, v(-34.84, -36.62) * mm, v(-36.14, -33.72) * mm, v(-37.7, -29.05) * mm, v(-38.47, -26.27) * mm, v(-39.29, -22.7) * mm, v(-40.33, -18.8) * mm, v(-40.61, -16.55) * mm, v(-40.87, -14.05) * mm, v(-41.05, -12.44) * mm, v(-41.06, -12.4) * mm], "startDerivative": vector(-9.23, -171.99) * mm, "endDerivative": vector(-18.47, 7.81) * mm});
            skFitSpline(sketch, "E23", {"points": [v(-38.2, -16.5) * mm, v(-38.71, -15.57) * mm, v(-39.05, -16.6) * mm], "startDerivative": vector(-0.95, 2.5) * mm, "endDerivative": vector(0.84, -2.53) * mm});
            skSolve(sketch);
        }
        {
            var Q0;
            Q0 = qSketchRegion(id + "F2", true);
            extrude(context, id + "F3", {"entities" : qUnion([Q0]), "depth" : 2 * mm, "offsetDistance" : 25 * mm});
        }
    });
